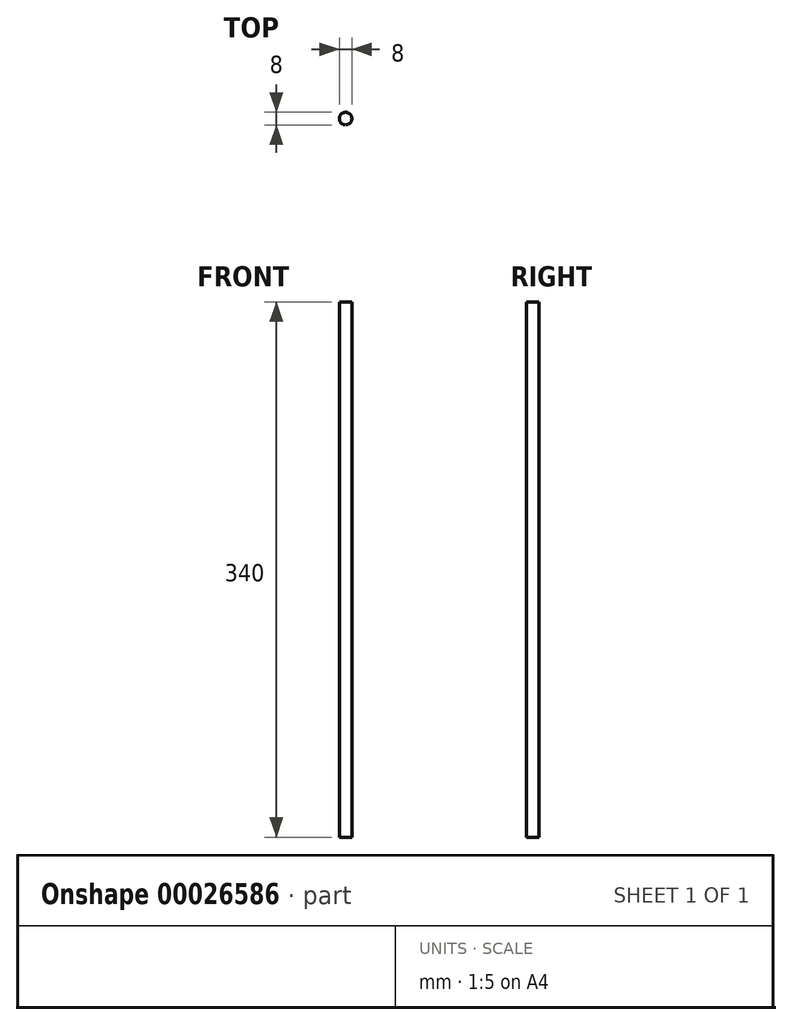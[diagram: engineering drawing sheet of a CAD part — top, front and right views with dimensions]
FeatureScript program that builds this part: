
annotation { "Feature Type Name" : "Feature", "Feature Type Description" : "" }
export const myFeature = defineFeature(function(context is Context, id is Id, definition is map)
    precondition{}
    {
        {
            var Q0;
            Q0=qCreatedBy(makeId("Top.planeOp"),FACE);
            var sketch = newSketch(context, id + "F0", { "sketchPlane" : qUnion([Q0])});
            skCircle(sketch, "E0", {"center": v(0, 0) * mm, "radius": 4 * mm});
            skSolve(sketch);
        }
        {
            var Q0;
            Q0=qSketchRegion(id+"F0",true);
            extrude(context, id + "F1", {"entities" : qUnion([Q0]), "depth" : 340 * mm});
        }
    });
